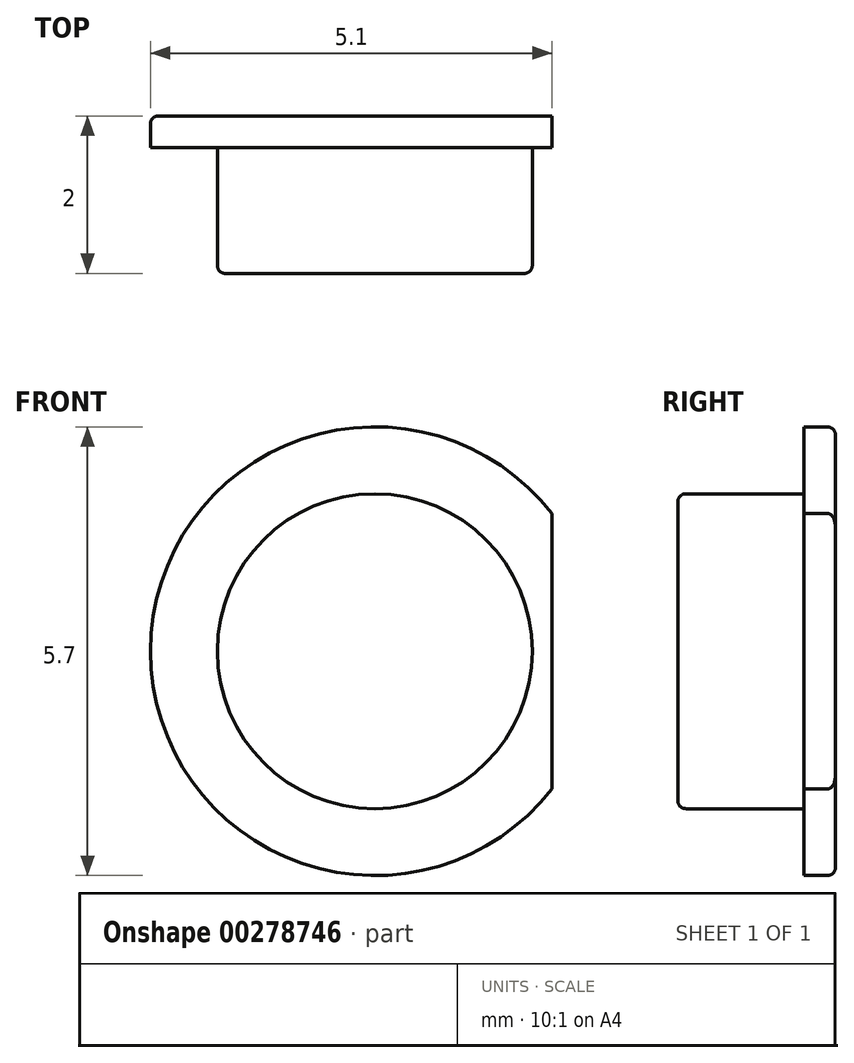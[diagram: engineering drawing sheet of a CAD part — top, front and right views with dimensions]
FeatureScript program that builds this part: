
annotation { "Feature Type Name" : "Feature", "Feature Type Description" : "" }
export const myFeature = defineFeature(function(context is Context, id is Id, definition is map)
    precondition{}
    {
        {
            var Q0;
            Q0=qCreatedBy(makeId("Front.planeOp"),FACE);
            var sketch = newSketch(context, id + "F0", { "sketchPlane" : qUnion([Q0])});
            skCircle(sketch, "E0", {"center": v(0, 0) * mm, "radius": 2.85 * mm});
            skSolve(sketch);
        }
        {
            var Q0;
            Q0 = qSketchRegion(id + "F0", true);
            extrude(context, id + "F1", {"entities" : qUnion([Q0]), "depth" : .4 * mm});
        }
        {
            var Q0;
            Q0=makeQuery(id+"F1.opExtrude","CAP_FACE",FACE,{"disambiguationData":[OSD([sQuery(id+"F0.wireOp",EDGE,"E0")])],"isStart":false});
            var sketch = newSketch(context, id + "F2", { "sketchPlane" : qUnion([Q0])});
            skCircle(sketch, "E1", {"center": v(0, 0) * mm, "radius": 2 * mm});
            skSolve(sketch);
        }
        {
            var Q0;
            Q0 = qSketchRegion(id + "F2", true);
            extrude(context, id + "F3", {"entities" : qUnion([Q0]), "operationType" : NewBodyOperationType.ADD, "depth" : 1.6 * mm});
        }
        {
            var Q0;
            Q0=makeQuery(id+"F3.opExtrude","CAP_EDGE",EDGE,{"disambiguationData":[OSD([sQuery(id+"F2.wireOp",EDGE,"E1")])],"isStart":false});
            var Q1;
            Q1=makeQuery(id+"F1.opExtrude","CAP_EDGE",EDGE,{"disambiguationData":[OSD([sQuery(id+"F0.wireOp",EDGE,"E0")])],"isStart":true});
            fillet(context, id + "F4", {"entities" : qUnion([Q0, Q1]), "radius" : 0.1 * mm, "tangentPropagation" : true, "allowEdgeOverflow" : false});
        }
        {
            var Q0;
            Q0=makeQuery(id+"F1.opExtrude","CAP_FACE",FACE,{"disambiguationData":[OSD([sQuery(id+"F0.wireOp",EDGE,"E0")])],"isStart":true});
            var sketch = newSketch(context, id + "F5", { "sketchPlane" : qUnion([Q0])});
            skArc(sketch, "E2.0", {"start": v(-2.25, 1.75) * mm, "mid": v(-2.85, 0) * mm, "end": v(-2.25, -1.75) * mm});
            skLineSegment(sketch, "E3", {"start": v(-2.25, 1.75) * mm, "end": v(-2.25, -1.75) * mm});
            skSolve(sketch);
        }
        {
            var Q0;
            Q0 = qSketchRegion(id + "F5", true);
            extrude(context, id + "F6", {"entities" : qUnion([Q0]), "operationType" : NewBodyOperationType.REMOVE, "oppositeDirection" : true, "depth" : 25 * mm});
        }
    });
